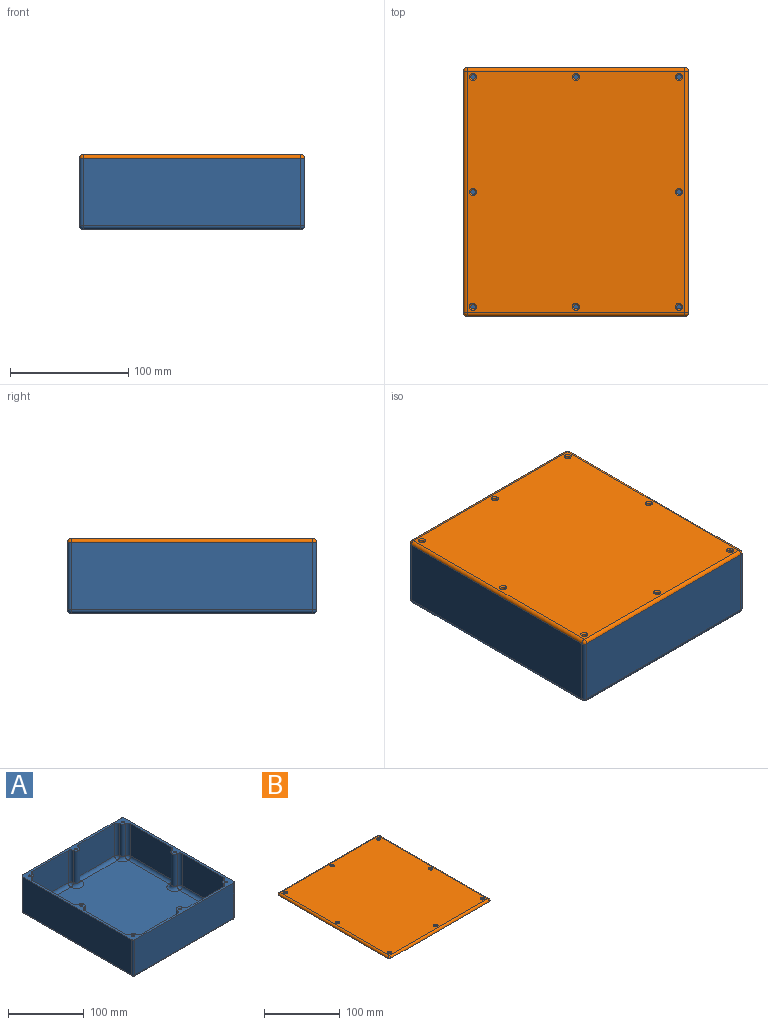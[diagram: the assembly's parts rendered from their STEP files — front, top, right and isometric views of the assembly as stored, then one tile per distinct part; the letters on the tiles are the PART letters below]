
ASSEMBLY  parts=2 mates=1
PART A: 99 faces, bbox 190x210x60 mm
  f0: plane 67x52mm, normal (0,1,0), area 3484mm2, adj f9,f66,f67,f70
  f1: plane 194x174mm, normal (0,0,1), area 32813.5mm2, adj f15,f19,f22,f27,f30,f32,f36,f42
  f2: plane 67x52mm, normal (0,1,0), area 3484mm2, adj f9,f52,f55,f59
  f3: plane 77x52mm, normal (-1,0,0), area 4004mm2, adj f9,f54,f58,f63
  f4: plane 77x52mm, normal (1,0,0), area 4004mm2, adj f9,f38,f42,f46
  f5: plane 67x52mm, normal (0,-1,0), area 3484mm2, adj f9,f26,f30,f35
  f6: plane 77x52mm, normal (-1,0,0), area 4004mm2, adj f9,f39,f43,f48
  f7: plane 67x52mm, normal (0,-1,0), area 3484mm2, adj f9,f15,f18,f20
  f8: plane 77x52mm, normal (1,0,0), area 4004mm2, adj f9,f24,f27,f31
  f9: plane 210x190mm, normal (0,0,1), area 3077.2mm2, adj f0,f2,f3,f4,f5,f6,f7,f8
  f10: plane 184x57mm, normal (0,1,0), area 10488mm2, adj f9,f76,f80,f82
  f11: plane 204x57mm, normal (-1,0,0), area 11628mm2, adj f9,f73,f79,f82
  f12: plane 184x57mm, normal (0,-1,0), area 10488mm2, adj f9,f71,f73,f74
  f13: plane 204x57mm, normal (1,0,0), area 11628mm2, adj f9,f71,f75,f76
  f14: plane 204x184mm, normal (0,0,-1), area 37536mm2, adj f74,f75,f79,f80
  f15: cylinder r=5mm len=67mm, axis (-1,0,0), area 526.2mm2, adj f1,f7,f16,f17
  f16: sphere r=5mm, area 39.3mm2, adj f15,f18,f22
  f17: sphere r=5mm, area 39.3mm2, adj f15,f19,f20
  f18: cylinder r=5mm len=52mm, axis (0,0,1), area 408.4mm2, adj f7,f9,f16,f21
  f19: torus R=10mm, axis (0,0,1), area 168.2mm2, adj f1,f17,f23,f28
  f20: cylinder r=5mm len=52mm, axis (0,0,-1), area 408.4mm2, adj f7,f9,f17,f23
  f21: cylinder r=5mm len=52mm, axis (0,0,1), area 408.4mm2, adj f9,f18,f22,f24
  f22: torus R=10mm, axis (0,0,1), area 84.1mm2, adj f1,f16,f21,f25
  f23: cylinder r=5mm len=52mm, axis (0,0,-1), area 816.8mm2, adj f9,f19,f20,f26
  f24: cylinder r=5mm len=52mm, axis (0,0,1), area 408.4mm2, adj f8,f9,f21,f25
  f25: sphere r=5mm, area 39.3mm2, adj f22,f24,f27
  f26: cylinder r=5mm len=52mm, axis (0,0,1), area 408.4mm2, adj f5,f9,f23,f28
  f27: cylinder r=5mm len=77mm, axis (0,-1,0), area 604.8mm2, adj f1,f8,f25,f29
  f28: sphere r=5mm, area 39.3mm2, adj f19,f26,f30
  f29: sphere r=5mm, area 39.3mm2, adj f27,f31,f32
  f30: cylinder r=5mm len=67mm, axis (-1,0,0), area 526.2mm2, adj f1,f5,f28,f33
  f31: cylinder r=5mm len=52mm, axis (0,0,-1), area 408.4mm2, adj f8,f9,f29,f34
  f32: torus R=10mm, axis (0,0,1), area 168.2mm2, adj f1,f29,f34,f40
  f33: sphere r=5mm, area 39.3mm2, adj f30,f35,f36
  f34: cylinder r=5mm len=52mm, axis (0,0,-1), area 816.8mm2, adj f9,f31,f32,f38
  f35: cylinder r=5mm len=52mm, axis (0,0,-1), area 408.4mm2, adj f5,f9,f33,f37
  f36: torus R=10mm, axis (0,0,1), area 84.1mm2, adj f1,f33,f37,f41
  f37: cylinder r=5mm len=52mm, axis (0,0,1), area 408.4mm2, adj f9,f35,f36,f39
  f38: cylinder r=5mm len=52mm, axis (0,0,1), area 408.4mm2, adj f4,f9,f34,f40
  f39: cylinder r=5mm len=52mm, axis (0,0,1), area 408.4mm2, adj f6,f9,f37,f41
  f40: sphere r=5mm, area 39.3mm2, adj f32,f38,f42
  f41: sphere r=5mm, area 39.3mm2, adj f36,f39,f43
  f42: cylinder r=5mm len=77mm, axis (0,-1,0), area 604.8mm2, adj f1,f4,f40,f44
  f43: cylinder r=5mm len=77mm, axis (0,1,0), area 604.8mm2, adj f1,f6,f41,f45
  f44: sphere r=5mm, area 39.3mm2, adj f42,f46,f50
  f45: sphere r=5mm, area 39.3mm2, adj f43,f47,f48
  f46: cylinder r=5mm len=52mm, axis (0,0,-1), area 408.4mm2, adj f4,f9,f44,f49
  f47: torus R=10mm, axis (0,0,1), area 168.2mm2, adj f1,f45,f51,f56
  f48: cylinder r=5mm len=52mm, axis (0,0,-1), area 408.4mm2, adj f6,f9,f45,f51
  f49: cylinder r=5mm len=52mm, axis (0,0,1), area 408.4mm2, adj f9,f46,f50,f52
  f50: torus R=10mm, axis (0,0,1), area 84.1mm2, adj f1,f44,f49,f53
  f51: cylinder r=5mm len=52mm, axis (0,0,-1), area 816.8mm2, adj f9,f47,f48,f54
  f52: cylinder r=5mm len=52mm, axis (0,0,1), area 408.4mm2, adj f2,f9,f49,f53
  f53: sphere r=5mm, area 39.3mm2, adj f50,f52,f55
  f54: cylinder r=5mm len=52mm, axis (0,0,1), area 408.4mm2, adj f3,f9,f51,f56
  f55: cylinder r=5mm len=67mm, axis (1,0,0), area 526.2mm2, adj f1,f2,f53,f57
  f56: sphere r=5mm, area 39.3mm2, adj f47,f54,f58
  f57: sphere r=5mm, area 39.3mm2, adj f55,f59,f60
  f58: cylinder r=5mm len=77mm, axis (0,1,0), area 604.8mm2, adj f1,f3,f56,f61
  f59: cylinder r=5mm len=52mm, axis (0,0,-1), area 408.4mm2, adj f2,f9,f57,f62
  f60: torus R=10mm, axis (0,0,1), area 168.2mm2, adj f1,f57,f62,f68
  f61: sphere r=5mm, area 39.3mm2, adj f58,f63,f64
  f62: cylinder r=5mm len=52mm, axis (0,0,-1), area 816.8mm2, adj f9,f59,f60,f66
  f63: cylinder r=5mm len=52mm, axis (0,0,-1), area 408.4mm2, adj f3,f9,f61,f65
  f64: torus R=10mm, axis (0,0,1), area 84.1mm2, adj f1,f61,f65,f69
  f65: cylinder r=5mm len=52mm, axis (0,0,1), area 408.4mm2, adj f9,f63,f64,f67
  f66: cylinder r=5mm len=52mm, axis (0,0,1), area 408.4mm2, adj f0,f9,f62,f68
  f67: cylinder r=5mm len=52mm, axis (0,0,-1), area 408.4mm2, adj f0,f9,f65,f69
  f68: sphere r=5mm, area 39.3mm2, adj f60,f66,f70
  f69: sphere r=5mm, area 39.3mm2, adj f64,f67,f70
  f70: cylinder r=5mm len=67mm, axis (1,0,0), area 526.2mm2, adj f0,f1,f68,f69
  f71: cylinder r=3mm len=57mm, axis (0,0,1), area 268.6mm2, adj f9,f12,f13,f72
  f72: sphere r=3mm, area 14.1mm2, adj f71,f74,f75
  f73: cylinder r=3mm len=57mm, axis (0,0,-1), area 268.6mm2, adj f9,f11,f12,f77
  f74: cylinder r=3mm len=184mm, axis (1,0,0), area 867.1mm2, adj f12,f14,f72,f77
  f75: cylinder r=3mm len=204mm, axis (0,1,0), area 961.3mm2, adj f13,f14,f72,f78
  f76: cylinder r=3mm len=57mm, axis (0,0,-1), area 268.6mm2, adj f9,f10,f13,f78
  f77: sphere r=3mm, area 14.1mm2, adj f73,f74,f79
  f78: sphere r=3mm, area 14.1mm2, adj f75,f76,f80
  f79: cylinder r=3mm len=204mm, axis (0,-1,0), area 961.3mm2, adj f11,f14,f77,f81
  f80: cylinder r=3mm len=184mm, axis (-1,0,0), area 867.1mm2, adj f10,f14,f78,f81
  f81: sphere r=3mm, area 14.1mm2, adj f79,f80,f82
  f82: cylinder r=3mm len=57mm, axis (0,0,1), area 268.6mm2, adj f9,f10,f11,f81
  f83: cylinder r=2mm len=15mm, axis (0,0,1), area 188.5mm2, adj f9,f84
  f84: plane 4x4mm, normal (0,0,1), area 12.6mm2, adj f83
  f85: cylinder r=2mm len=15mm, axis (0,0,1), area 188.5mm2, adj f9,f86
  f86: plane 4x4mm, normal (0,0,1), area 12.6mm2, adj f85
  f87: cylinder r=2mm len=15mm, axis (0,0,1), area 188.5mm2, adj f9,f88
  f88: plane 4x4mm, normal (0,0,1), area 12.6mm2, adj f87
  f89: cylinder r=2mm len=15mm, axis (0,0,1), area 188.5mm2, adj f9,f90
  f90: plane 4x4mm, normal (0,0,1), area 12.6mm2, adj f89
  f91: cylinder r=2mm len=15mm, axis (0,0,1), area 188.5mm2, adj f9,f92
  f92: plane 4x4mm, normal (0,0,1), area 12.6mm2, adj f91
  f93: cylinder r=2mm len=15mm, axis (0,0,1), area 188.5mm2, adj f9,f94
  f94: plane 4x4mm, normal (0,0,1), area 12.6mm2, adj f93
  f95: cylinder r=2mm len=15mm, axis (0,0,1), area 188.5mm2, adj f9,f96
  f96: plane 4x4mm, normal (0,0,1), area 12.6mm2, adj f95
  f97: cylinder r=2mm len=15mm, axis (0,0,1), area 188.5mm2, adj f9,f98
  f98: plane 4x4mm, normal (0,0,1), area 12.6mm2, adj f97
PART B: 26 faces, bbox 190x210x3 mm
  f0: plane 204x184mm, normal (0,0,1), area 37309.8mm2, adj f3,f4,f7,f8,f18,f19,f20,f21
  f1: plane 210x190mm, normal (0,0,-1), area 39791.7mm2, adj f2,f3,f4,f5,f6,f7,f8,f9
  f2: sphere r=3mm, area 14.1mm2, adj f1,f3,f4
  f3: cylinder r=3mm len=204mm, axis (0,-1,0), area 961.3mm2, adj f0,f1,f2,f5
  f4: cylinder r=3mm len=184mm, axis (-1,0,0), area 867.1mm2, adj f0,f1,f2,f6
  f5: sphere r=3mm, area 14.1mm2, adj f1,f3,f7
  f6: sphere r=3mm, area 14.1mm2, adj f1,f4,f8
  f7: cylinder r=3mm len=184mm, axis (1,0,0), area 867.1mm2, adj f0,f1,f5,f9
  f8: cylinder r=3mm len=204mm, axis (0,1,0), area 961.3mm2, adj f0,f1,f6,f9
  f9: sphere r=3mm, area 14.1mm2, adj f1,f7,f8
  f10: cylinder r=2mm len=4mm, axis (0,0,-1), area 25.1mm2, adj f1,f25
  f11: cylinder r=2mm len=4mm, axis (0,0,-1), area 25.1mm2, adj f1,f18
  f12: cylinder r=2mm len=4mm, axis (0,0,-1), area 25.1mm2, adj f1,f19
  f13: cylinder r=2mm len=4mm, axis (0,0,-1), area 25.1mm2, adj f1,f20
  f14: cylinder r=2mm len=4mm, axis (0,0,-1), area 25.1mm2, adj f1,f21
  f15: cylinder r=2mm len=4mm, axis (0,0,-1), area 25.1mm2, adj f1,f22
  f16: cylinder r=2mm len=4mm, axis (0,0,-1), area 25.1mm2, adj f1,f23
  f17: cylinder r=2mm len=4mm, axis (0,0,-1), area 25.1mm2, adj f1,f24
  f18: cone r=2mm half-angle=45deg, axis (0,0,1), area 22.2mm2, adj f0,f11
  f19: cone r=2mm half-angle=45deg, axis (0,0,1), area 22.2mm2, adj f0,f12
  f20: cone r=2mm half-angle=45deg, axis (0,0,1), area 22.2mm2, adj f0,f13
  f21: cone r=2mm half-angle=45deg, axis (0,0,1), area 22.2mm2, adj f0,f14
  f22: cone r=2mm half-angle=45deg, axis (0,0,1), area 22.2mm2, adj f0,f15
  f23: cone r=2mm half-angle=45deg, axis (0,0,1), area 22.2mm2, adj f0,f16
  f24: cone r=2mm half-angle=45deg, axis (0,0,1), area 22.2mm2, adj f0,f17
  f25: cone r=2mm half-angle=45deg, axis (0,0,1), area 22.2mm2, adj f0,f10
PLACE A t=(-34.63,29.52,-60)mm
PLACE B at identity
MATE slider A.f49 <-> B.f12  axis (0,0,1) through (-90.03,-96.45,0)mm
